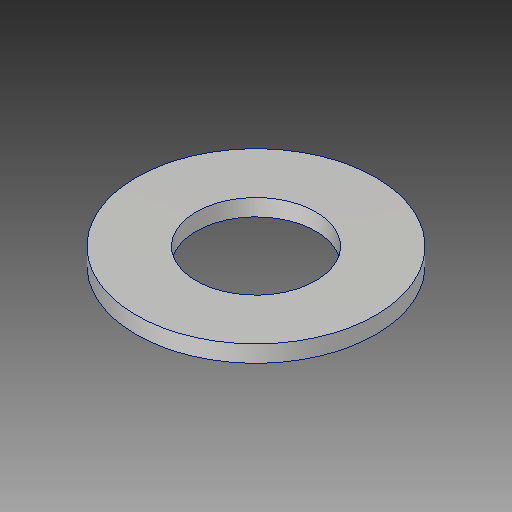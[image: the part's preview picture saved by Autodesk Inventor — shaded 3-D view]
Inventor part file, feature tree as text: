
AUTODESK INVENTOR PART (.ipt)
format: ipt  version: 2017 (Build 210142000, 142)  size: 88,064 bytes
history: native  units: in
note: dims shown in document units (in); Inventor stores cm internally (conversion verified against a paired STEP export)
features: extrude x1, sketch x1
ambient origin geometry x8: Origin, YZ Plane, XZ Plane, XY Plane, X Axis, Y Axis, Z Axis, Center Point
bodies: Solid1 (feature_tree)
feature tree (2):
  extrude  "Extrusion1"  Depth=0.035in
  sketch  "Sketch1"  dims[d0=0.25in d1=0.5in d2=0.035in d3=0.0in]
